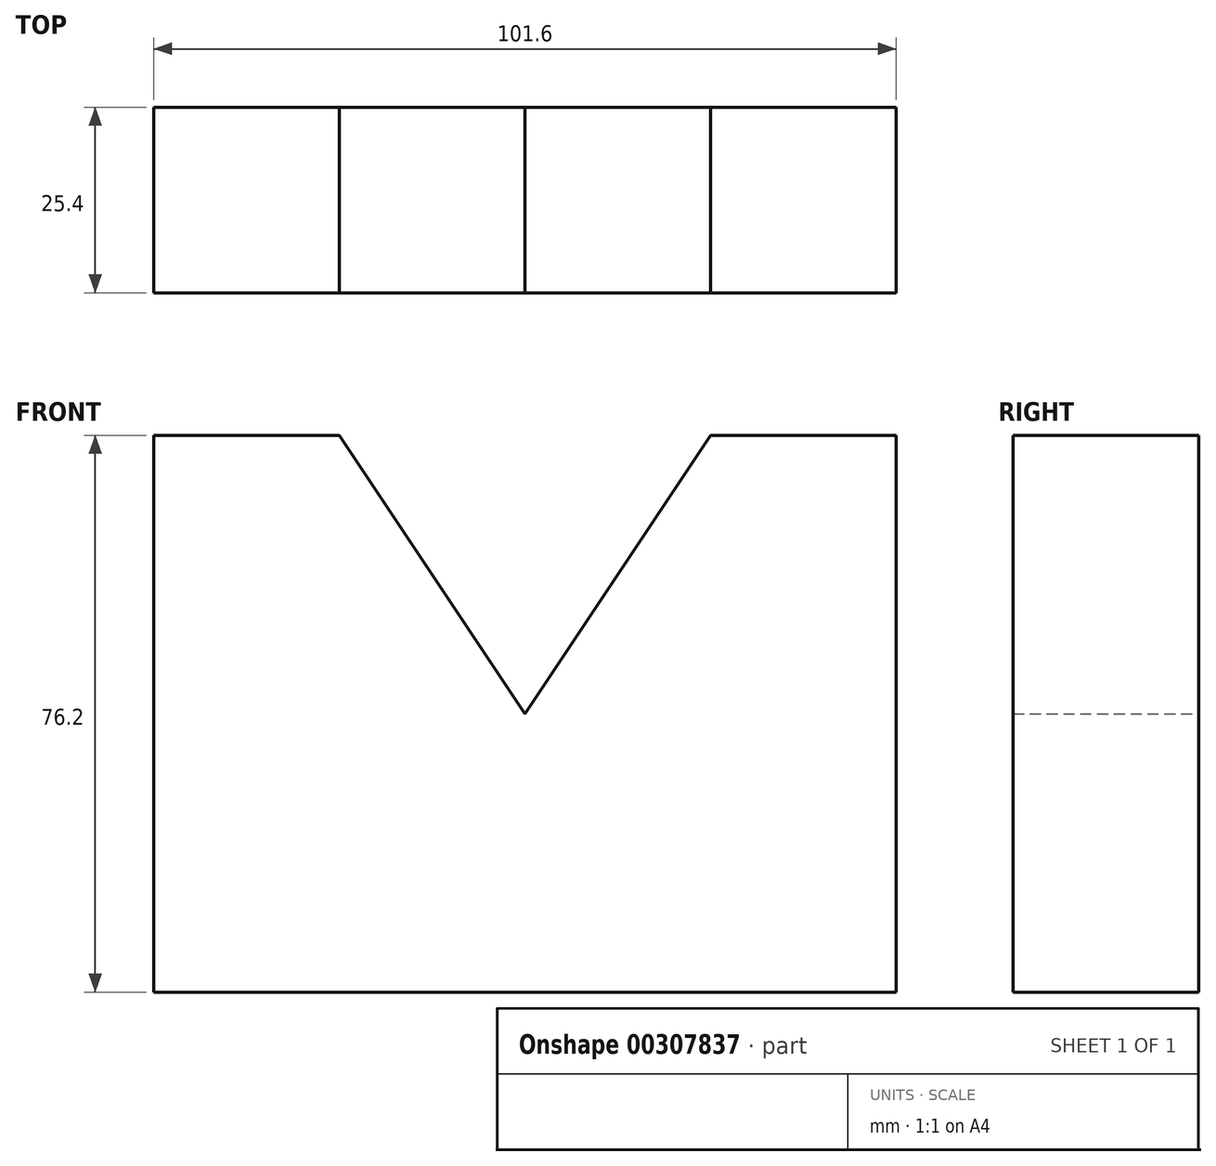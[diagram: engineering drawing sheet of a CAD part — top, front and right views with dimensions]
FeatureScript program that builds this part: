
annotation { "Feature Type Name" : "Feature", "Feature Type Description" : "" }
export const myFeature = defineFeature(function(context is Context, id is Id, definition is map)
    precondition{}
    {
        {
            var Q0;
            Q0=qCreatedBy(makeId("Front.planeOp"),FACE);
            var sketch = newSketch(context, id + "F0", { "sketchPlane" : qUnion([Q0])});
            skLineSegment(sketch, "E0", {"start": v(-46.83, -49.6) * mm, "end": v(54.77, -49.6) * mm});
            skLineSegment(sketch, "E1", {"start": v(-46.83, -49.6) * mm, "end": v(-46.83, 26.6) * mm});
            skLineSegment(sketch, "E2", {"start": v(-46.83, 26.6) * mm, "end": v(-21.43, 26.6) * mm});
            skLineSegment(sketch, "E3", {"start": v(54.77, -49.6) * mm, "end": v(54.77, 26.6) * mm});
            skLineSegment(sketch, "E4", {"start": v(54.77, 26.6) * mm, "end": v(29.37, 26.6) * mm});
            skLineSegment(sketch, "E5", {"start": v(-21.43, 26.6) * mm, "end": v(3.97, -11.5) * mm});
            skLineSegment(sketch, "E6", {"start": v(29.37, 26.6) * mm, "end": v(3.97, -11.5) * mm});
            skSolve(sketch);
        }
        {
            var Q0;
            Q0=makeQuery(id+"F0.imprint","IMPRINT",FACE,{"disambiguationData":[TD([[makeQuery(id+"F0.imprint","IMPRINT",EDGE,{"derivedFrom":sQuery(id+"F0.wireOp",EDGE,"E0")}),1.0]])]});
            extrude(context, id + "F1", {"entities" : qUnion([Q0]), "depth" : 25.4 * mm});
        }
    });
